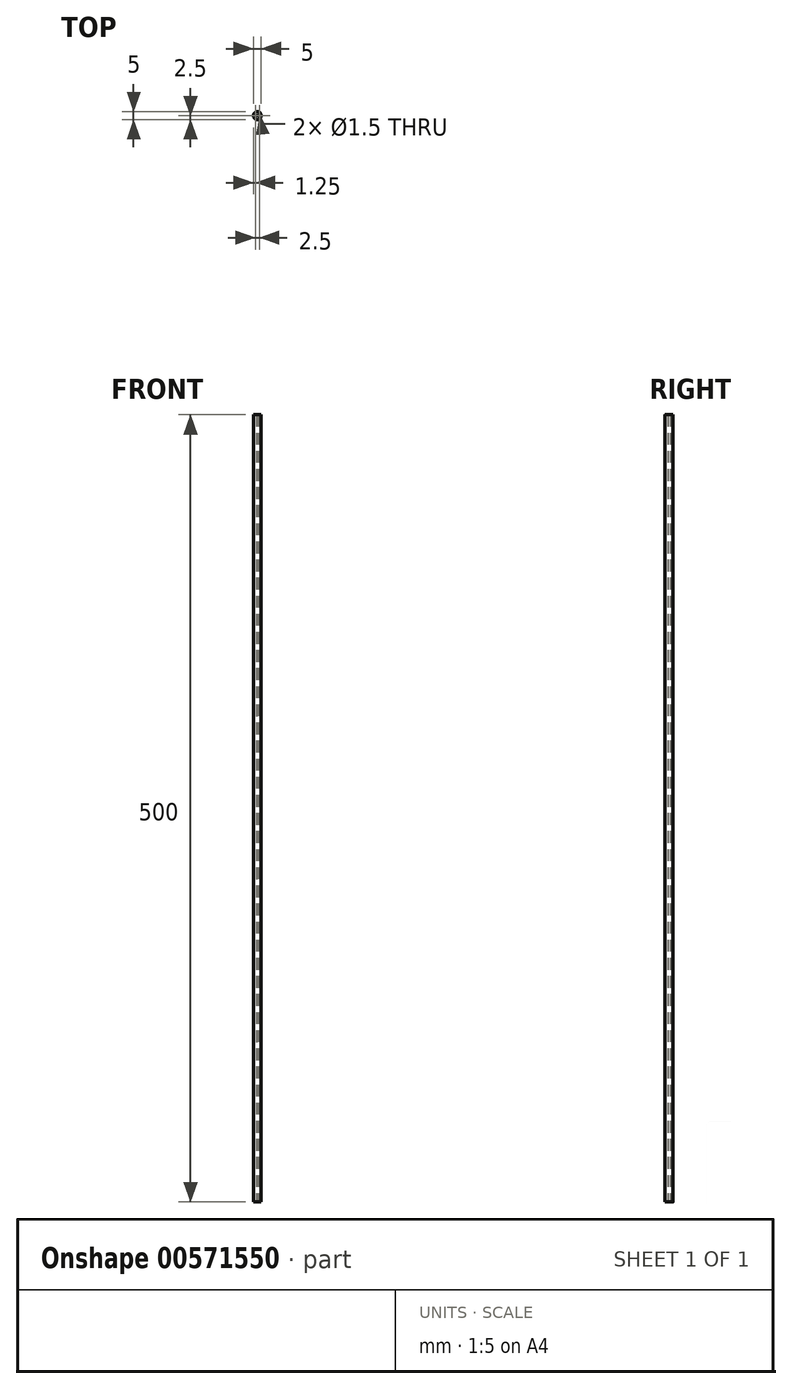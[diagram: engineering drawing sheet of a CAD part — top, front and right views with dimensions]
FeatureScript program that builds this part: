
annotation { "Feature Type Name" : "Feature", "Feature Type Description" : "" }
export const myFeature = defineFeature(function(context is Context, id is Id, definition is map)
    precondition{}
    {
        {
            var Q0;
            Q0=qCreatedBy(makeId("Top.planeOp"),FACE);
            var sketch = newSketch(context, id + "F0", { "sketchPlane" : qUnion([Q0])});
            skCircle(sketch, "E0", {"center": v(0, 0) * mm, "radius": 2.5 * mm});
            skCircle(sketch, "E1", {"center": v(1.25, 0) * mm, "radius": 0.75 * mm});
            skCircle(sketch, "E2", {"center": v(-1.25, 0) * mm, "radius": 0.75 * mm});
            skSolve(sketch);
        }
        {
            var Q0;
            Q0=makeQuery(id+"F0.imprint","IMPRINT",FACE,{"disambiguationData":[TD([[makeQuery(id+"F0.imprint","IMPRINT",EDGE,{"derivedFrom":sQuery(id+"F0.wireOp",EDGE,"E0")}),1.0]])]});
            extrude(context, id + "F1", {"entities" : qUnion([Q0]), "depth" : 500 * mm, "offsetDistance" : 25 * mm});
        }
    });
